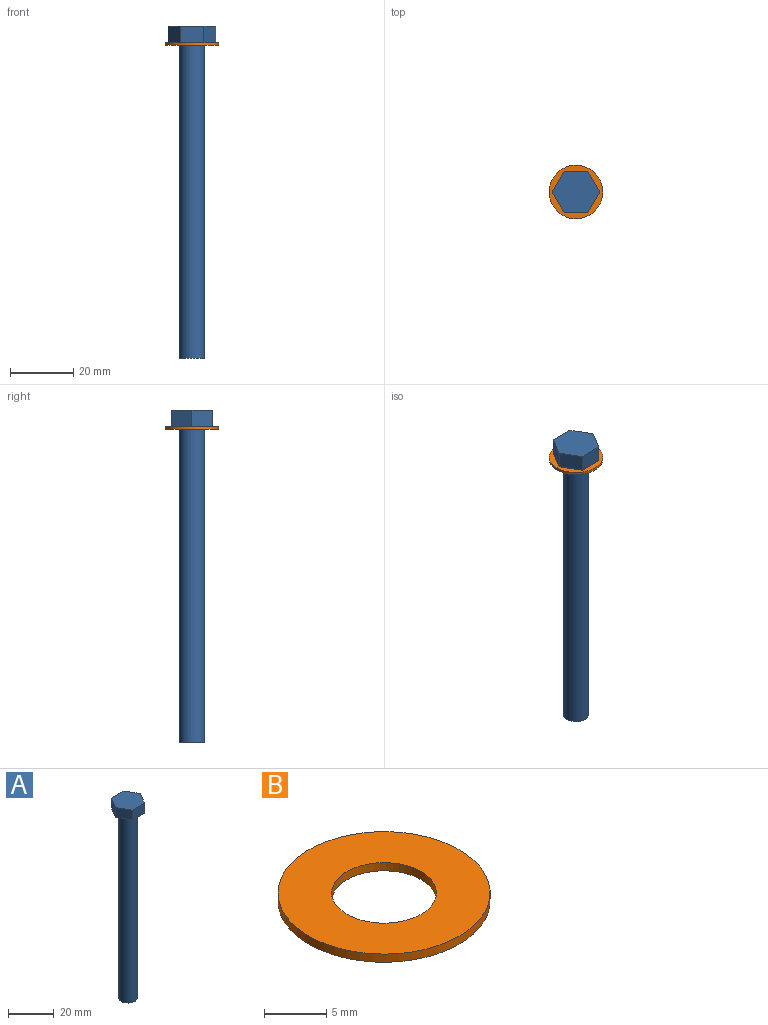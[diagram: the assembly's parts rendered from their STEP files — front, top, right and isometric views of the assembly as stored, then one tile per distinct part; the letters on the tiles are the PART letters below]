
ASSEMBLY  parts=2 mates=1
PART A: 10 faces, bbox 15x13x105.3 mm
  f0: plane 6.5x5.3mm, normal (0.87,-0.5,0), area 39.8mm2, adj f1,f5,f6,f7
  f1: plane 6.5x5.3mm, normal (0.87,0.5,0), area 39.8mm2, adj f0,f2,f6,f7
  f2: plane 7.51x5.3mm, normal (0,1,0), area 39.8mm2, adj f1,f3,f6,f7
  f3: plane 6.5x5.3mm, normal (-0.87,0.5,0), area 39.8mm2, adj f2,f4,f6,f7
  f4: plane 6.5x5.3mm, normal (-0.87,-0.5,0), area 39.8mm2, adj f3,f5,f6,f7
  f5: plane 7.51x5.3mm, normal (0,-1,0), area 39.8mm2, adj f0,f4,f6,f7
  f6: plane 15.01x13mm, normal (0,0,1), area 146.4mm2, adj f0,f1,f2,f3,f4,f5
  f7: plane 15.01x13mm, normal (0,0,-1), area 96.1mm2, adj f0,f1,f2,f3,f4,f5,f8
  f8: cylinder r=4mm len=100mm, axis (0,0,1), area 2513.3mm2, adj f7,f9
  f9: plane 8x8mm, normal (0,0,-1), area 50.3mm2, adj f8
PART B: 4 faces, bbox 17x17x0.8 mm
  f0: cylinder r=4.2mm len=8.4mm, axis (0,0,-1), area 21.1mm2, adj f2,f3
  f1: cylinder r=8.5mm len=17mm, axis (0,0,-1), area 42.7mm2, adj f2,f3
  f2: plane 17x17mm, normal (0,0,1), area 171.6mm2, adj f0,f1
  f3: plane 17x17mm, normal (0,0,-1), area 171.6mm2, adj f0,f1
PLACE A t=(-985.56,-162.37,-17.76)mm
PLACE B rot(axis=(1,0,0),180deg) t=(-926.36,210.23,-17.76)mm
MATE fastened B.f0 <-> A.f8  axis (0,0,1) through (131.82,32.7,-17.76)mm
